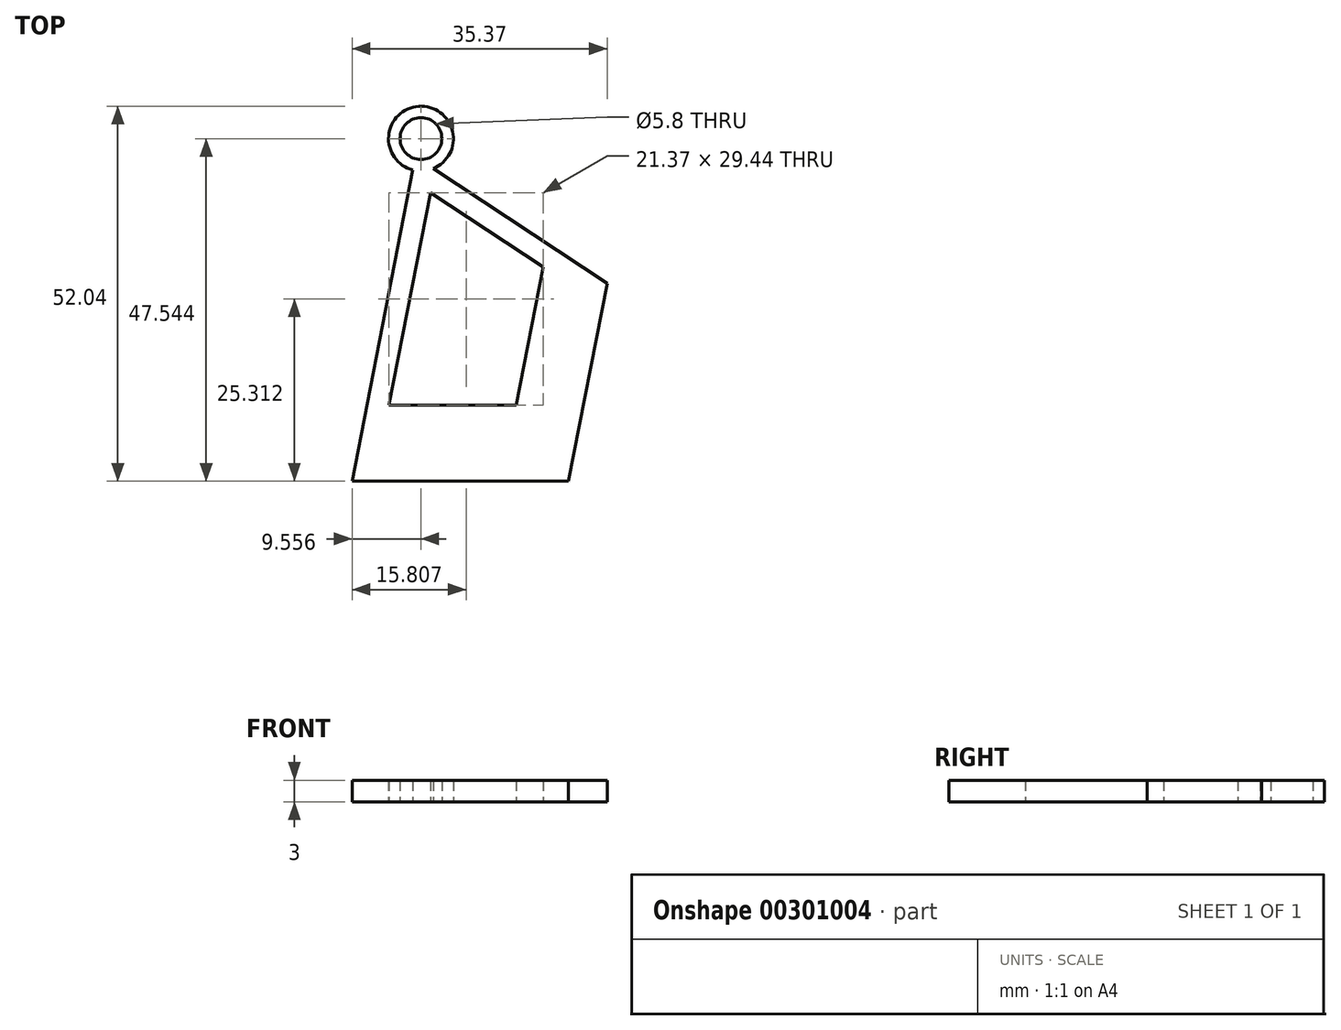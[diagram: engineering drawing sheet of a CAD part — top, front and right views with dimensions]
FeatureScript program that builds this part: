
annotation { "Feature Type Name" : "Feature", "Feature Type Description" : "" }
export const myFeature = defineFeature(function(context is Context, id is Id, definition is map)
    precondition{}
    {
        {
            var Q0;
            Q0=qCreatedBy(makeId("Top.planeOp"),FACE);
            var sketch = newSketch(context, id + "F0", { "sketchPlane" : qUnion([Q0])});
            skLineSegment(sketch, "E0", {"start": v(0, 34.41) * mm, "end": v(0, -10.59) * mm});
            skLineSegment(sketch, "E1", {"start": v(0, 34.41) * mm, "end": v(-8.8, -10.59) * mm});
            skLineSegment(sketch, "E2", {"start": v(-8.8, -10.59) * mm, "end": v(21.2, -10.59) * mm});
            skLineSegment(sketch, "E3", {"start": v(21.2, -10.59) * mm, "end": v(26.58, 16.9) * mm});
            skLineSegment(sketch, "E4", {"start": v(26.58, 16.9) * mm, "end": v(0, 34.41) * mm});
            skLineSegment(sketch, "E5", {"start": v(2.09, 29.44) * mm, "end": v(-3.67, 0) * mm});
            skLineSegment(sketch, "E6", {"start": v(-3.67, 0) * mm, "end": v(13.96, 0) * mm});
            skCircle(sketch, "E7", {"center": v(0.77, 36.95) * mm, "radius": 4.5 * mm});
            skLineSegment(sketch, "E8", {"start": v(2.09, 29.44) * mm, "end": v(17.7, 19.15) * mm});
            skLineSegment(sketch, "E9", {"start": v(17.7, 19.15) * mm, "end": v(13.96, 0) * mm});
            skSolve(sketch);
        }
        {
            var Q0;
            {var subQ3=sQuery(id+"F0.wireOp",EDGE,"E3");Q0=makeQuery(id+"F0.imprint","IMPRINT",FACE,{"disambiguationData":[TD([[makeQuery(id+"F0.imprint","IMPRINT",EDGE,{"derivedFrom":subQ3}),1.0]])]});}
            var Q1;
            {var subQ3=sQuery(id+"F0.wireOp",EDGE,"E7");var subQ5=sQuery(id+"F0.wireOp",EDGE,"E0");var subQ9=makeQuery(id+"F0.imprint","INTERSECT",VERTEX,{"derivedFrom":[subQ5,subQ3]});Q1=makeQuery(id+"F0.imprint","IMPRINT",FACE,{"disambiguationData":[TD([[makeQuery(id+"F0.imprint","IMPRINT",EDGE,{"disambiguationData":[TD([[subQ9,-1.0]])],"derivedFrom":subQ5}),-1.0]])]});}
            var Q2;
            {var subQ1=sQuery(id+"F0.wireOp",EDGE,"E1");var subQ3=sQuery(id+"F0.wireOp",EDGE,"E7");var subQ4=makeQuery(id+"F0.imprint","INTERSECT",VERTEX,{"derivedFrom":[subQ1,subQ3]});Q2=makeQuery(id+"F0.imprint","IMPRINT",FACE,{"disambiguationData":[TD([[makeQuery(id+"F0.imprint","IMPRINT",EDGE,{"disambiguationData":[TD([[subQ4,1.0]])],"derivedFrom":subQ3}),1.0]])]});}
            var Q3;
            {var subQ0=sQuery(id+"F0.wireOp",EDGE,"E4");var subQ3=sQuery(id+"F0.wireOp",EDGE,"E7");var subQ5=makeQuery(id+"F0.imprint","INTERSECT",VERTEX,{"derivedFrom":[subQ0,subQ3]});Q3=makeQuery(id+"F0.imprint","IMPRINT",FACE,{"disambiguationData":[TD([[makeQuery(id+"F0.imprint","IMPRINT",EDGE,{"disambiguationData":[TD([[subQ5,1.0]])],"derivedFrom":subQ3}),1.0]])]});}
            var Q4;
            {var subQ0=sQuery(id+"F0.wireOp",EDGE,"E1");var subQ3=sQuery(id+"F0.wireOp",EDGE,"E7");var subQ5=makeQuery(id+"F0.imprint","INTERSECT",VERTEX,{"derivedFrom":[subQ0,subQ3]});Q4=makeQuery(id+"F0.imprint","IMPRINT",FACE,{"disambiguationData":[TD([[makeQuery(id+"F0.imprint","IMPRINT",EDGE,{"disambiguationData":[TD([[subQ5,-1.0]])],"derivedFrom":subQ3}),1.0]])]});}
            extrude(context, id + "F1", {"entities" : qUnion([Q0, Q1, Q2, Q3, Q4]), "depth" : 3 * mm, "offsetDistance" : 25 * mm});
        }
        {
            var Q0;
            Q0=sQuery(id+"F0.wireOp",VERTEX,"E7.center");
            var Q1;
            Q1=makeQuery(id+"F1.opExtrude","SWEPT_BODY",BODY,{"disambiguationData":[OSD([sQuery(id+"F0.wireOp",EDGE,"E1"),sQuery(id+"F0.wireOp",EDGE,"E2"),sQuery(id+"F0.wireOp",EDGE,"E3"),sQuery(id+"F0.wireOp",EDGE,"E4"),sQuery(id+"F0.wireOp",EDGE,"E5"),sQuery(id+"F0.wireOp",EDGE,"E6"),sQuery(id+"F0.wireOp",EDGE,"MudtsU7s-pa9p-5QJq-Xm2w-Z2SFyE6b6GAi"),sQuery(id+"F0.wireOp",EDGE,"dbbIoJ7B-JExe-d3Py-UFgL-0nyB5KJbkYbo"),sQuery(id+"F0.wireOp",EDGE,"E7")])]});
            hole(context, id + "F2", {"style" : HoleStyle.SIMPLE, "endStyle" : HoleEndStyle.BLIND, "oppositeDirection" : true, "holeDiameter" : 5.8 * mm, "majorDiameter" : 5 * mm, "holeDepth" : 3 * mm, "isTappedThrough" : true, "tappedDepth" : 12 * mm, "tapClearance" : 3, "locations" : qUnion([Q0]), "scope" : qUnion([Q1])});
        }
    });
